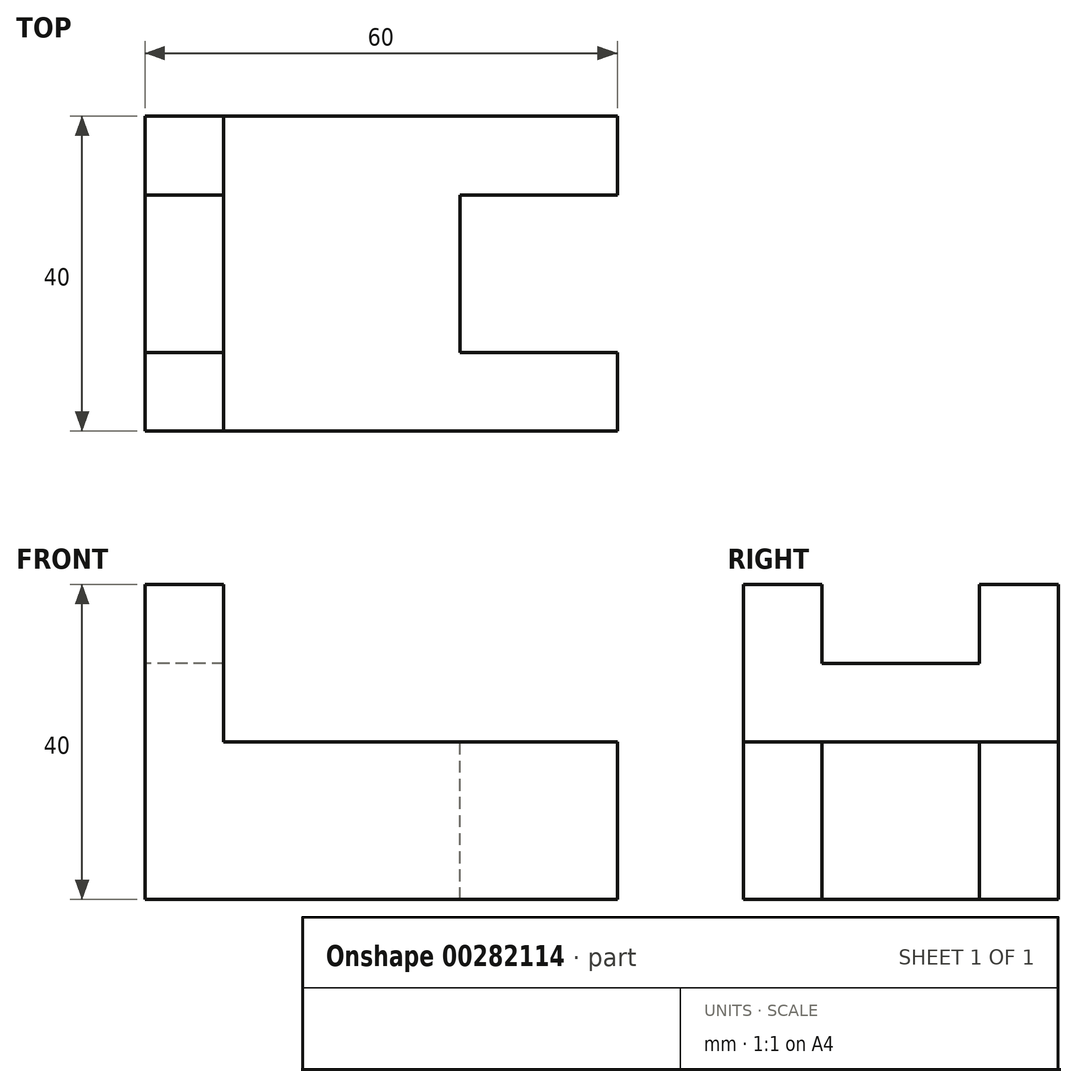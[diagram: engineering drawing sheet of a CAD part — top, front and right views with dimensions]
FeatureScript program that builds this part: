
annotation { "Feature Type Name" : "Feature", "Feature Type Description" : "" }
export const myFeature = defineFeature(function(context is Context, id is Id, definition is map)
    precondition{}
    {
        {
            var Q0;
            Q0=qCreatedBy(makeId("Top.planeOp"),FACE);
            var sketch = newSketch(context, id + "F0", { "sketchPlane" : qUnion([Q0])});
            skLineSegment(sketch, "E0.bottom", {"start": v(-37.43, 0) * mm, "end": v(22.57, 0) * mm});
            skLineSegment(sketch, "E0.top", {"start": v(-37.43, 40) * mm, "end": v(22.57, 40) * mm});
            skLineSegment(sketch, "E0.left", {"start": v(-37.43, 0) * mm, "end": v(-37.43, 40) * mm});
            skLineSegment(sketch, "E0.right", {"start": v(22.57, 0) * mm, "end": v(22.57, 40) * mm});
            skSolve(sketch);
        }
        {
            var Q0;
            Q0 = qSketchRegion(id + "F0", true);
            extrude(context, id + "F1", {"entities" : qUnion([Q0]), "depth" : 20 * mm});
        }
        {
            var Q0;
            Q0=makeQuery(id+"F1.opExtrude","CAP_FACE",FACE,{"disambiguationData":[OSD([sQuery(id+"F0.wireOp",EDGE,"E0.bottom"),sQuery(id+"F0.wireOp",EDGE,"E0.top"),sQuery(id+"F0.wireOp",EDGE,"E0.left"),sQuery(id+"F0.wireOp",EDGE,"E0.right")])],"isStart":false});
            var sketch = newSketch(context, id + "F2", { "sketchPlane" : qUnion([Q0])});
            skSolve(sketch);
        }
        {
            var Q0;
            Q0=makeQuery(id+"F2.imprint","IMPRINT",FACE,{"disambiguationData":[TD([[makeQuery(id+"F2.imprint","IMPRINT",EDGE,{"derivedFrom":makeQuery(id+"F1.opExtrude","CAP_EDGE",EDGE,{"disambiguationData":[OSD([sQuery(id+"F0.wireOp",EDGE,"E0.bottom")])],"isStart":false})}),1.0]])]});
            var sketch = newSketch(context, id + "F3", { "sketchPlane" : qUnion([Q0])});
            skLineSegment(sketch, "E1", {"start": v(-37.43, 40) * mm, "end": v(-27.43, 40) * mm});
            skLineSegment(sketch, "E2", {"start": v(-27.43, 40) * mm, "end": v(-27.43, 0) * mm});
            skLineSegment(sketch, "E3", {"start": v(-27.43, 0) * mm, "end": v(-37.43, 0) * mm});
            skLineSegment(sketch, "E4", {"start": v(-37.43, 0) * mm, "end": v(-37.43, 40) * mm});
            skSolve(sketch);
        }
        {
            var Q0;
            Q0 = qSketchRegion(id + "F3", true);
            extrude(context, id + "F4", {"entities" : qUnion([Q0]), "operationType" : NewBodyOperationType.ADD, "depth" : 20 * mm});
        }
        {
            var Q0;
            Q0=makeQuery(id+"F2.imprint","IMPRINT",FACE,{"disambiguationData":[TD([[makeQuery(id+"F2.imprint","IMPRINT",EDGE,{"derivedFrom":makeQuery(id+"F1.opExtrude","CAP_EDGE",EDGE,{"disambiguationData":[OSD([sQuery(id+"F0.wireOp",EDGE,"E0.bottom")])],"isStart":false})}),1.0]])]});
            var sketch = newSketch(context, id + "F5", { "sketchPlane" : qUnion([Q0])});
            skLineSegment(sketch, "E5.bottom", {"start": v(22.57, 30) * mm, "end": v(2.57, 30) * mm});
            skLineSegment(sketch, "E5.top", {"start": v(22.57, 10) * mm, "end": v(2.57, 10) * mm});
            skLineSegment(sketch, "E5.left", {"start": v(22.57, 30) * mm, "end": v(22.57, 10) * mm});
            skLineSegment(sketch, "E5.right", {"start": v(2.57, 30) * mm, "end": v(2.57, 10) * mm});
            skSolve(sketch);
        }
        {
            var Q0;
            Q0=makeQuery(id+"F5.imprint","IMPRINT",FACE,{"disambiguationData":[TD([[makeQuery(id+"F5.imprint","IMPRINT",EDGE,{"derivedFrom":sQuery(id+"F5.wireOp",EDGE,"E5.bottom")}),1.0]])]});
            extrude(context, id + "F6", {"entities" : qUnion([Q0]), "operationType" : NewBodyOperationType.REMOVE, "endBound" : BoundingType.THROUGH_ALL, "oppositeDirection" : true, "depth" : 25 * mm});
        }
        {
            var Q0;
            Q0=makeQuery(id+"F4.opExtrude","CAP_FACE",FACE,{"disambiguationData":[OSD([sQuery(id+"F3.wireOp",EDGE,"E1"),sQuery(id+"F3.wireOp",EDGE,"E2"),sQuery(id+"F3.wireOp",EDGE,"E3"),sQuery(id+"F3.wireOp",EDGE,"E4")])],"isStart":false});
            var sketch = newSketch(context, id + "F7", { "sketchPlane" : qUnion([Q0])});
            skLineSegment(sketch, "E6.bottom", {"start": v(-27.43, 30) * mm, "end": v(-37.43, 30) * mm});
            skLineSegment(sketch, "E6.top", {"start": v(-27.43, 10) * mm, "end": v(-37.43, 10) * mm});
            skLineSegment(sketch, "E6.left", {"start": v(-27.43, 30) * mm, "end": v(-27.43, 10) * mm});
            skLineSegment(sketch, "E6.right", {"start": v(-37.43, 30) * mm, "end": v(-37.43, 10) * mm});
            skSolve(sketch);
        }
        {
            var Q0;
            Q0=makeQuery(id+"F7.imprint","IMPRINT",FACE,{"disambiguationData":[TD([[makeQuery(id+"F7.imprint","IMPRINT",EDGE,{"derivedFrom":sQuery(id+"F7.wireOp",EDGE,"E6.bottom")}),1.0]])]});
            extrude(context, id + "F8", {"entities" : qUnion([Q0]), "operationType" : NewBodyOperationType.REMOVE, "oppositeDirection" : true, "depth" : 10 * mm});
        }
    });
